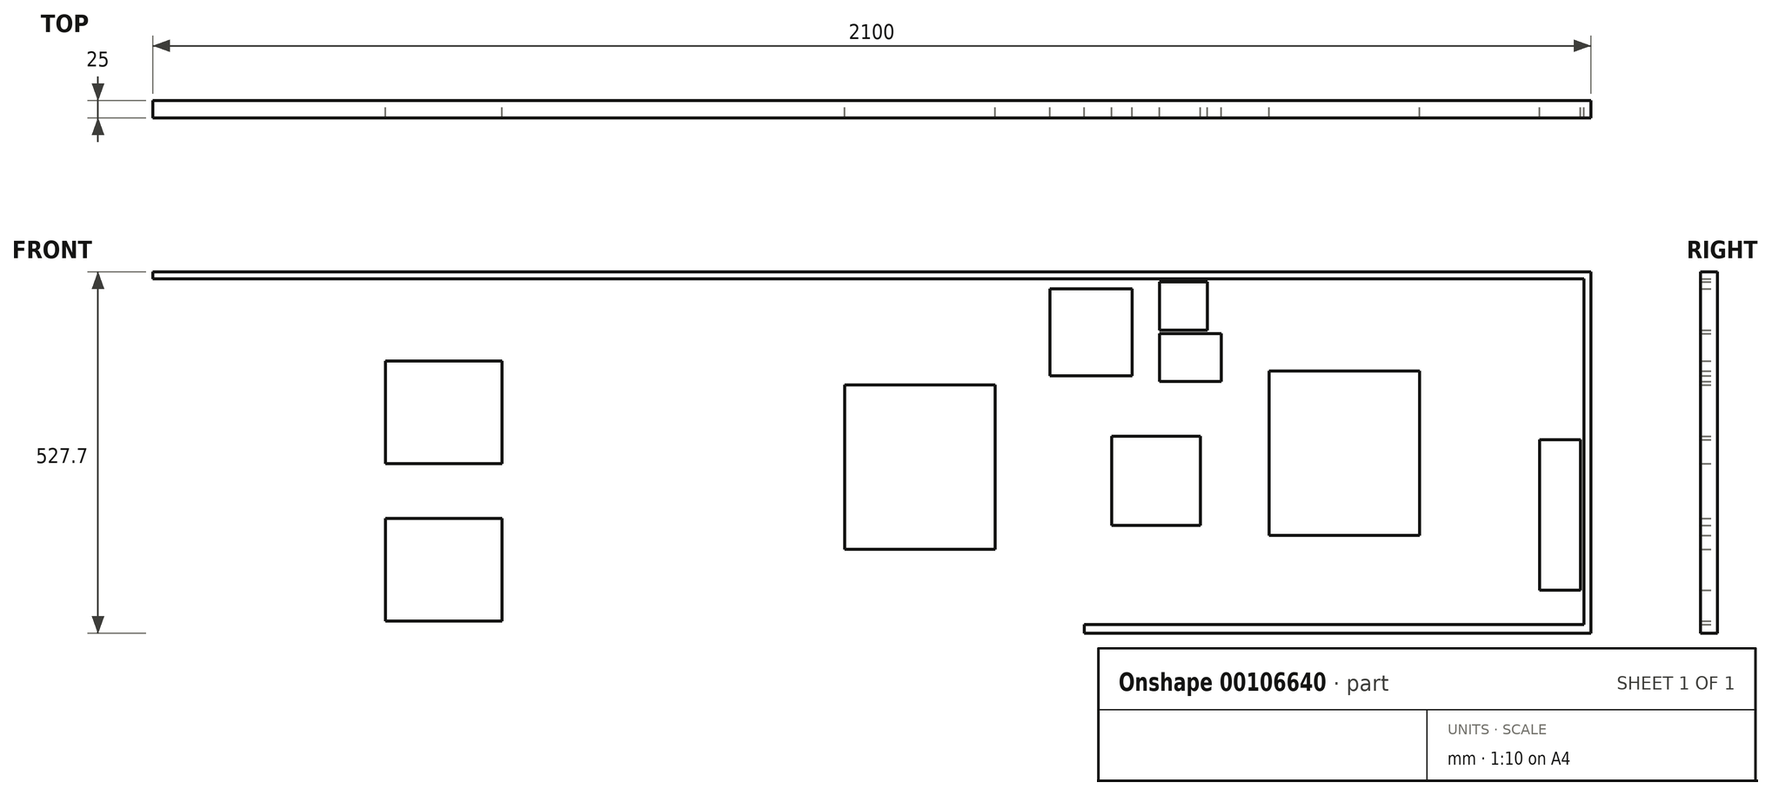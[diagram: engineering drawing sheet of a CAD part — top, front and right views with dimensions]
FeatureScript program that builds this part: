
annotation { "Feature Type Name" : "Feature", "Feature Type Description" : "" }
export const myFeature = defineFeature(function(context is Context, id is Id, definition is map)
    precondition{}
    {
        {
            var Q0;
            Q0=qCreatedBy(makeId("Front.planeOp"),FACE);
            var sketch = newSketch(context, id + "F0", { "sketchPlane" : qUnion([Q0])});
            skLineSegment(sketch, "E0.bottom", {"start": v(220, -120) * mm, "end": v(0, -120) * mm});
            skLineSegment(sketch, "E0.top", {"start": v(220, 120) * mm, "end": v(0, 120) * mm});
            skLineSegment(sketch, "E0.left", {"start": v(220, -120) * mm, "end": v(220, 120) * mm});
            skLineSegment(sketch, "E0.right", {"start": v(0, -120) * mm, "end": v(0, 120) * mm});
            skPoint(sketch, "E0.middle", {"position": v(110, 0) * mm});
            skLineSegment(sketch, "E1.bottom", {"start": v(470, 255) * mm, "end": v(-1630, 255) * mm});
            skLineSegment(sketch, "E1.top", {"start": v(470, 265) * mm, "end": v(-1630, 265) * mm});
            skLineSegment(sketch, "E1.left", {"start": v(470, 255) * mm, "end": v(470, 265) * mm});
            skLineSegment(sketch, "E1.right", {"start": v(-1630, 255) * mm, "end": v(-1630, 265) * mm});
            skLineSegment(sketch, "E2.bottom", {"start": v(-230, 25) * mm, "end": v(-100, 25) * mm});
            skLineSegment(sketch, "E2.top", {"start": v(-230, -105) * mm, "end": v(-100, -105) * mm});
            skLineSegment(sketch, "E2.left", {"start": v(-230, 25) * mm, "end": v(-230, -105) * mm});
            skLineSegment(sketch, "E2.right", {"start": v(-100, 25) * mm, "end": v(-100, -105) * mm});
            skLineSegment(sketch, "E3.bottom", {"start": v(-320, 240) * mm, "end": v(-200, 240) * mm});
            skLineSegment(sketch, "E3.top", {"start": v(-320, 113) * mm, "end": v(-200, 113) * mm});
            skLineSegment(sketch, "E3.left", {"start": v(-320, 240) * mm, "end": v(-320, 113) * mm});
            skLineSegment(sketch, "E3.right", {"start": v(-200, 240) * mm, "end": v(-200, 113) * mm});
            skLineSegment(sketch, "E4.bottom", {"start": v(-160, 175) * mm, "end": v(-70, 175) * mm});
            skLineSegment(sketch, "E4.top", {"start": v(-160, 105) * mm, "end": v(-70, 105) * mm});
            skLineSegment(sketch, "E4.left", {"start": v(-160, 175) * mm, "end": v(-160, 105) * mm});
            skLineSegment(sketch, "E4.right", {"start": v(-70, 175) * mm, "end": v(-70, 105) * mm});
            skLineSegment(sketch, "E5.bottom", {"start": v(-160, 250) * mm, "end": v(-90, 250) * mm});
            skLineSegment(sketch, "E5.top", {"start": v(-160, 180) * mm, "end": v(-90, 180) * mm});
            skLineSegment(sketch, "E5.left", {"start": v(-160, 250) * mm, "end": v(-160, 180) * mm});
            skLineSegment(sketch, "E5.right", {"start": v(-90, 250) * mm, "end": v(-90, 180) * mm});
            skLineSegment(sketch, "E6.bottom", {"start": v(-270, -250) * mm, "end": v(470, -250) * mm});
            skLineSegment(sketch, "E6.top", {"start": v(-270, -262.7) * mm, "end": v(470, -262.7) * mm});
            skLineSegment(sketch, "E6.left", {"start": v(-270, -250) * mm, "end": v(-270, -262.7) * mm});
            skLineSegment(sketch, "E6.right", {"start": v(470, -250) * mm, "end": v(470, -262.7) * mm});
            skLineSegment(sketch, "E7.bottom", {"start": v(470, 265) * mm, "end": v(460, 265) * mm});
            skLineSegment(sketch, "E7.top", {"start": v(470, -262.7) * mm, "end": v(460, -262.7) * mm});
            skLineSegment(sketch, "E7.left", {"start": v(470, 265) * mm, "end": v(470, -262.7) * mm});
            skLineSegment(sketch, "E7.right", {"start": v(460, 265) * mm, "end": v(460, -262.7) * mm});
            skLineSegment(sketch, "E8.bottom", {"start": v(395, 20) * mm, "end": v(455, 20) * mm});
            skLineSegment(sketch, "E8.top", {"start": v(395, -200) * mm, "end": v(455, -200) * mm});
            skLineSegment(sketch, "E8.left", {"start": v(395, 20) * mm, "end": v(395, -200) * mm});
            skLineSegment(sketch, "E8.right", {"start": v(455, 20) * mm, "end": v(455, -200) * mm});
            skLineSegment(sketch, "E9.bottom", {"start": v(-400, -140) * mm, "end": v(-620, -140) * mm});
            skLineSegment(sketch, "E9.top", {"start": v(-400, 100) * mm, "end": v(-620, 100) * mm});
            skLineSegment(sketch, "E9.left", {"start": v(-400, -140) * mm, "end": v(-400, 100) * mm});
            skLineSegment(sketch, "E9.right", {"start": v(-620, -140) * mm, "end": v(-620, 100) * mm});
            skLineSegment(sketch, "E10.bottom", {"start": v(-1290, 135) * mm, "end": v(-1120, 135) * mm});
            skLineSegment(sketch, "E10.top", {"start": v(-1290, -15) * mm, "end": v(-1120, -15) * mm});
            skLineSegment(sketch, "E10.left", {"start": v(-1290, 135) * mm, "end": v(-1290, -15) * mm});
            skLineSegment(sketch, "E10.right", {"start": v(-1120, 135) * mm, "end": v(-1120, -15) * mm});
            skLineSegment(sketch, "E11.bottom", {"start": v(-1290, -95) * mm, "end": v(-1120, -95) * mm});
            skLineSegment(sketch, "E11.top", {"start": v(-1290, -245) * mm, "end": v(-1120, -245) * mm});
            skLineSegment(sketch, "E11.left", {"start": v(-1290, -95) * mm, "end": v(-1290, -245) * mm});
            skLineSegment(sketch, "E11.right", {"start": v(-1120, -95) * mm, "end": v(-1120, -245) * mm});
            skSolve(sketch);
        }
        {
            var Q0;
            Q0=qSketchRegion(id+"F0",true);
            extrude(context, id + "F1", {"entities" : qUnion([Q0]), "depth" : 25 * mm});
        }
    });
